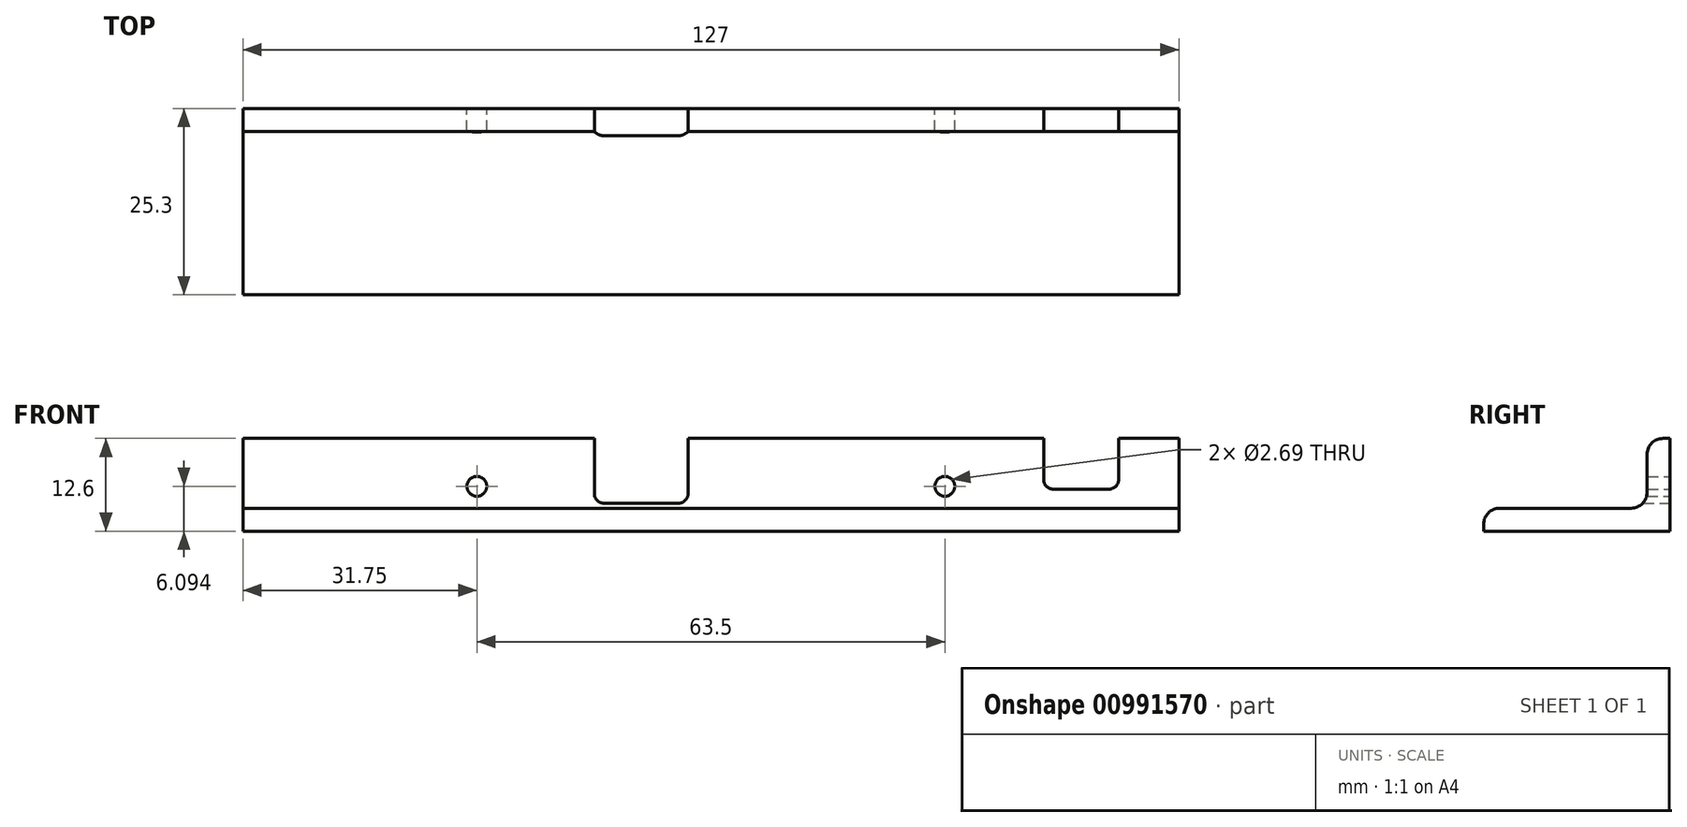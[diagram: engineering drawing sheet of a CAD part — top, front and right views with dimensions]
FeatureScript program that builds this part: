
annotation { "Feature Type Name" : "Feature", "Feature Type Description" : "" }
export const myFeature = defineFeature(function(context is Context, id is Id, definition is map)
    precondition{}
    {
        {
            var Q0;
            Q0=qCreatedBy(makeId("Right.planeOp"),FACE);
            var sketch = newSketch(context, id + "F0", { "sketchPlane" : qUnion([Q0])});
            skLineSegment(sketch, "E0", {"start": v(-10.29, -8.26) * mm, "end": v(15.01, -8.26) * mm});
            skLineSegment(sketch, "E1", {"start": v(15.01, -8.26) * mm, "end": v(15.01, 4.34) * mm});
            skLineSegment(sketch, "E2", {"start": v(15.01, 4.34) * mm, "end": v(14.05, 4.34) * mm});
            skLineSegment(sketch, "E3", {"start": v(11.89, 2.18) * mm, "end": v(11.89, -2.98) * mm});
            skLineSegment(sketch, "E4", {"start": v(9.73, -5.14) * mm, "end": v(-8.13, -5.14) * mm});
            skLineSegment(sketch, "E5", {"start": v(-10.29, -7.3) * mm, "end": v(-10.29, -8.26) * mm});
            skPoint(sketch, "E6.visualSharp", {"position": v(-10.29, -5.14) * mm});
            skArc(sketch, "E6.filletArc", {"start": v(-8.13, -5.14) * mm, "mid": v(-9.65, -5.77) * mm, "end": v(-10.29, -7.3) * mm});
            skPoint(sketch, "E7.visualSharp", {"position": v(11.89, 4.34) * mm});
            skArc(sketch, "E7.filletArc", {"start": v(14.05, 4.34) * mm, "mid": v(12.52, 3.7) * mm, "end": v(11.89, 2.18) * mm});
            skPoint(sketch, "E8.visualSharp", {"position": v(11.89, -5.14) * mm});
            skArc(sketch, "E8.filletArc", {"start": v(9.73, -5.14) * mm, "mid": v(11.26, -4.5) * mm, "end": v(11.89, -2.98) * mm});
            skSolve(sketch);
        }
        {
            var Q0;
            Q0 = qSketchRegion(id + "F0", true);
            extrude(context, id + "F1", {"entities" : qUnion([Q0]), "depth" : 127 * mm, "offsetDistance" : 25.4 * mm});
        }
        {
            var Q0;
            Q0=makeQuery(id+"F1.opExtrude","SWEPT_FACE",FACE,{"disambiguationData":[OSD([sQuery(id+"F0.wireOp",EDGE,"E1")])]});
            var sketch = newSketch(context, id + "F2", { "sketchPlane" : qUnion([Q0])});
            skCircle(sketch, "E9", {"center": v(-31.75, -2.17) * mm, "radius": 1.35 * mm});
            skCircle(sketch, "E10", {"center": v(-95.25, -2.17) * mm, "radius": 1.35 * mm});
            skSolve(sketch);
        }
        {
            var Q0;
            Q0 = qSketchRegion(id + "F2", true);
            extrude(context, id + "F3", {"entities" : qUnion([Q0]), "operationType" : NewBodyOperationType.REMOVE, "endBound" : BoundingType.THROUGH_ALL, "oppositeDirection" : true, "depth" : 25.4 * mm, "offsetDistance" : 25.4 * mm});
        }
        {
            var Q0;
            Q0=makeQuery(id+"F1.opExtrude","SWEPT_FACE",FACE,{"disambiguationData":[OSD([sQuery(id+"F0.wireOp",EDGE,"E1")])]});
            var sketch = newSketch(context, id + "F4", { "sketchPlane" : qUnion([Q0])});
            skLineSegment(sketch, "E11.bottom", {"start": v(-108.66, 4.34) * mm, "end": v(-118.82, 4.34) * mm});
            skLineSegment(sketch, "E11.top", {"start": v(-109.93, -2.55) * mm, "end": v(-117.55, -2.55) * mm});
            skLineSegment(sketch, "E11.left", {"start": v(-108.66, 4.34) * mm, "end": v(-108.66, -1.28) * mm});
            skLineSegment(sketch, "E11.right", {"start": v(-118.82, 4.34) * mm, "end": v(-118.82, -1.28) * mm});
            skLineSegment(sketch, "E12.bottom", {"start": v(-47.7, 4.34) * mm, "end": v(-60.4, 4.34) * mm});
            skLineSegment(sketch, "E12.top", {"start": v(-48.97, -4.45) * mm, "end": v(-59.13, -4.45) * mm});
            skLineSegment(sketch, "E12.left", {"start": v(-47.7, 4.34) * mm, "end": v(-47.7, -3.18) * mm});
            skLineSegment(sketch, "E12.right", {"start": v(-60.4, 4.34) * mm, "end": v(-60.4, -3.18) * mm});
            skPoint(sketch, "E13.visualSharp", {"position": v(-47.7, -4.45) * mm});
            skArc(sketch, "E13.filletArc", {"start": v(-48.97, -4.45) * mm, "mid": v(-48.07, -4.08) * mm, "end": v(-47.7, -3.18) * mm});
            skPoint(sketch, "E14.visualSharp", {"position": v(-60.4, -4.45) * mm});
            skArc(sketch, "E14.filletArc", {"start": v(-60.4, -3.18) * mm, "mid": v(-60.03, -4.08) * mm, "end": v(-59.13, -4.45) * mm});
            skPoint(sketch, "E15.visualSharp", {"position": v(-108.66, -2.55) * mm});
            skArc(sketch, "E15.filletArc", {"start": v(-109.93, -2.55) * mm, "mid": v(-109.03, -2.18) * mm, "end": v(-108.66, -1.28) * mm});
            skPoint(sketch, "E16.visualSharp", {"position": v(-118.82, -2.55) * mm});
            skArc(sketch, "E16.filletArc", {"start": v(-118.82, -1.28) * mm, "mid": v(-118.45, -2.18) * mm, "end": v(-117.55, -2.55) * mm});
            skSolve(sketch);
        }
        {
            var Q0;
            Q0 = qSketchRegion(id + "F4", true);
            extrude(context, id + "F5", {"entities" : qUnion([Q0]), "operationType" : NewBodyOperationType.REMOVE, "endBound" : BoundingType.THROUGH_ALL, "oppositeDirection" : true, "depth" : 25.4 * mm, "offsetDistance" : 25.4 * mm});
        }
    });
